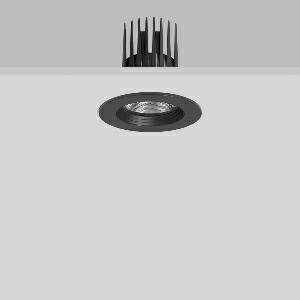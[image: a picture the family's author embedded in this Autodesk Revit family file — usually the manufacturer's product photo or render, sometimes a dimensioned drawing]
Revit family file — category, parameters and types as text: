
# Revit family: heledon_mini_e_901748_003_2_76_6565
name_source: partatom
category: Lighting Fixtures
units: mm (PartAtom-declared; Revit-internal decimal feet)

## family parameters
Cut with Voids When Loaded = No
Host = Face
Light Source = No
Part Type = Normal
Room Calculation Point = No
Round Connector Dimension = Use Diameter
Shared = No

## types (1)
- HELEDON mini E (1 x LED Modul 927, 3400 lm, 2700)
    Apparent Load = 29 VA
    Approval mark = CE
    CIE Flux Codes = 100 100 100 100 100
    Color Rendering = 92
    Color Temperature = 2700
    Default Elevation = 1800 mm
    Description = Series: HELEDON mini
Round recessed downlight. Housing: die-cast aluminium, powder-coated. Black plastic ring and recessed LED to prevent glare from the side. Optical assembly with reflector made of MIRO-Silver with 98% total light reflection for outstanding efficiency - can be changed without tools. Best colour rendering index Ra>90. Suitable for Recessed ceiling mounting. Installation without tools thanks to spring fastening system. Including separate LED converter with connecting cable 600 mm.High quality converter without flickering and stroboscopic effect. Through-wiring box (5 pole) available as accessory. The following accessories can be mounted without use of tools: interchangeable lenses, decorative glasses, honeycomb louvre, clear and frosted diffusers, white interchangeable plastic ring. 
Colour: deep black, matt (RAL 9005)
Diameter: 124 mm
Height: 3 mm
Cut-out diameter: 114 mm
Recess height: 170 mm
Luminaire: recess height: 120 mm
Lamp: LED
Socket: without socket
Colour temperature: 2700K
Colour rendering index (CRI): 92
System power: 29 W
Rated luminous flux: 3400 lm
Luminous efficiency: 117 lm/W
Control gear: Converter, dimmable, DALI
Protection class: II
Type of protection: IP 20
    Height = 0 mm  [stored 0 ft]
    Lamp = 1 x LED Modul 927
    Lamp Light Flux = 3400 lm
    Lamp count = 1
    Length = 124 mm  [stored 0.406824 ft]
    Lifetime = 50000 h
    Luminous efficacy = 117 lm/W
    Manufacturer = RZB
    ModVariant = No
    Model = 901748.003.2.76
    Mounting Place = Ceiling
    Mounting Type = Recessed
    Number of Poles = 1
    OnlyDefault = Yes
    Power Factor = 1
    Product Name = HELEDON mini E
    Product group = Recessed downlights
    ProductGroupID = 402
    Protection Class = Protection class II
    Protection Degree = IP 20
    RLX_Detail_Level = 1
    RLX_Emergency_Light_Flux = 0 lm
    RLX_Emergency_Type = 0
    RLX_Emergency_Type_DB = No
    RlxData = <blob elided: 127733 chars, md5=5e1fb1f2>
    Socket = socket
    Standby Power = 0 W
    System Light Flux = 3400 lm
    System Power = 29 W
    Type Comments = Product without accessories
    Type Image = 901657.003.jpg
    URL = http://relux.com
    VarID = ---
    Voltage = 230 V
    Voltage Range = 220-240 V
    Weight = 0.00 kg
    Width = 0 mm  [stored 0 ft]

note: [stored X ft] marks values corroborated as IEEE doubles in the binary element streams (Revit-internal decimal feet)

## geometry (parser evidence)
native form markers: Blend x4, Sweep x11
no freeform markers — native parametric forms only
